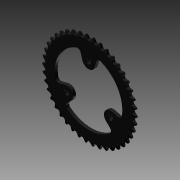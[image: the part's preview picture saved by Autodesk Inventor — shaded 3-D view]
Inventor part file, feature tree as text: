
AUTODESK INVENTOR PART (.ipt)
format: ipt  version: 2012 (Build 160160000, 160)  size: 1,118,720 bytes
history: native  units: in
note: dims shown in document units (in); Inventor stores cm internally (conversion verified against a paired STEP export)
features: boolean_combine x1, extrude x1, fillet x1, imported_body x1, sketch x1
ambient origin geometry x8: Origin, YZ Plane, XZ Plane, XY Plane, X Axis, Y Axis, Z Axis, Center Point
feature tree (5):
  boolean_combine  "Combine1"
  extrude  "Extrusion1"  TaperAngle=0.0deg  [1 undecoded]
  fillet  "Fillet1"  Radius=0.125in
  imported_body  "Base1"
  sketch  "Sketch1"  dims[d0=1.25in d1=0.0in d2=0.0in d3=0.125in]
note: 1 required parameter value undecoded (feature->parameter linkage not recoverable at this tier; creation-order binding heuristic only, values carry confidence <= 0.55)
